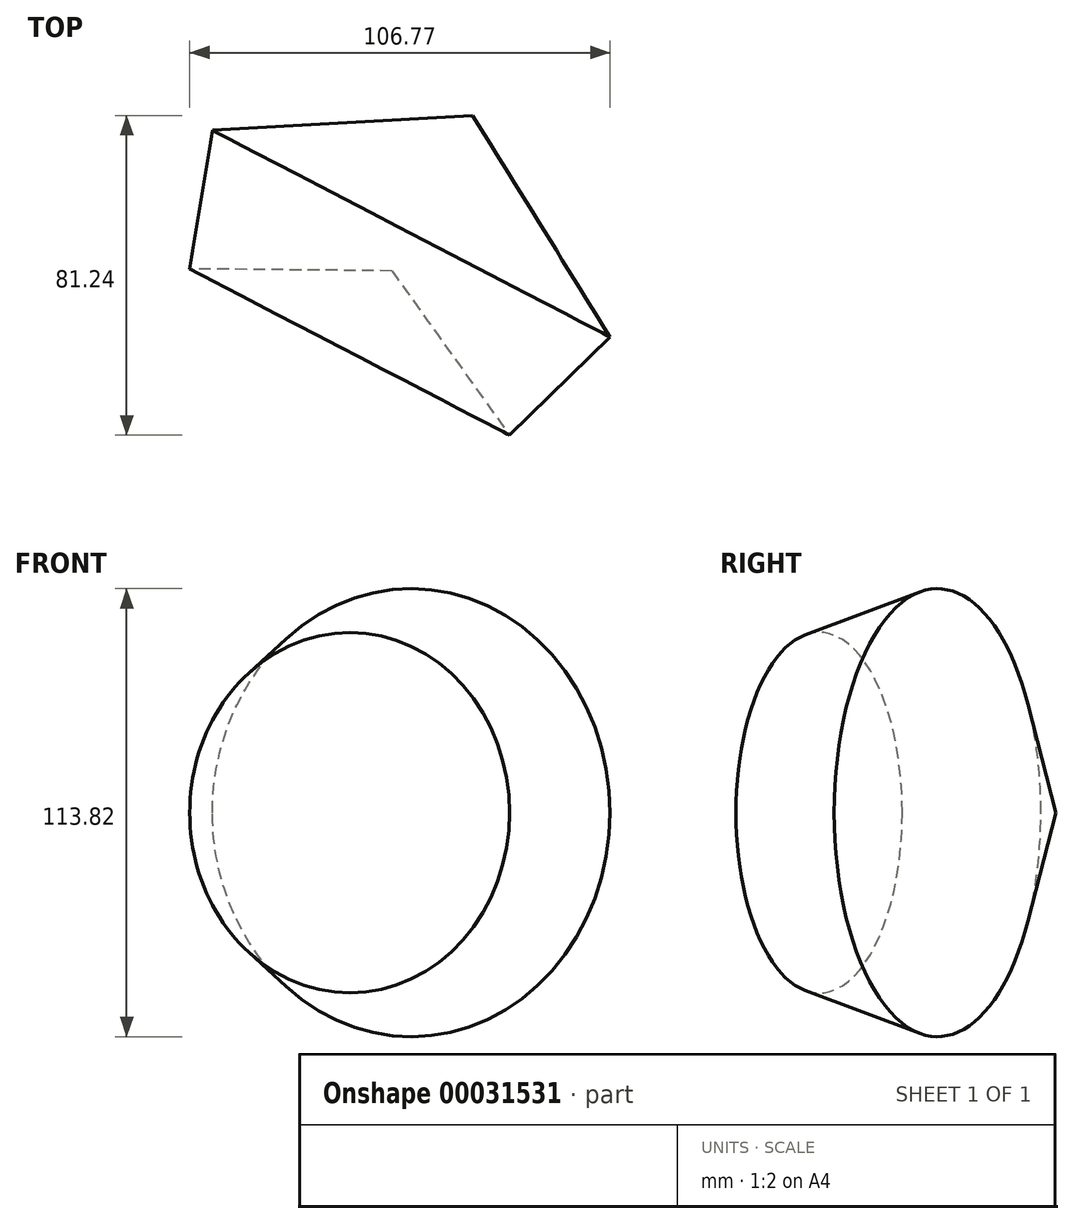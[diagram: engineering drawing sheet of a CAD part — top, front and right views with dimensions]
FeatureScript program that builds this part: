
annotation { "Feature Type Name" : "Feature", "Feature Type Description" : "" }
export const myFeature = defineFeature(function(context is Context, id is Id, definition is map)
    precondition{}
    {
        {
            var Q0;
            Q0=qCreatedBy(makeId("Top.planeOp"),FACE);
            var sketch = newSketch(context, id + "F0", { "sketchPlane" : qUnion([Q0])});
            skLineSegment(sketch, "E0", {"start": v(0, 0) * mm, "end": v(29.9, -41.75) * mm});
            skLineSegment(sketch, "E1", {"start": v(29.9, -41.75) * mm, "end": v(55.4, -16.8) * mm});
            skLineSegment(sketch, "E2", {"start": v(55.4, -16.8) * mm, "end": v(20.53, 39.49) * mm});
            skLineSegment(sketch, "E3", {"start": v(20.53, 39.49) * mm, "end": v(0, 0) * mm});
            skSolve(sketch);
        }
        {
            var Q0;
            Q0=makeQuery(id+"F0.imprint","IMPRINT",FACE,{"disambiguationData":[TD([[makeQuery(id+"F0.imprint","IMPRINT",EDGE,{"derivedFrom":sQuery(id+"F0.wireOp",EDGE,"E0")}),1.0]])]});
            var Q1;
            Q1=sQuery(id+"F0.wireOp",EDGE,"E3");
            revolve(context, id + "F1", {"entities" : qUnion([Q0]), "axis" : qUnion([Q1]), "revolveType" : RevolveType.FULL});
        }
    });
